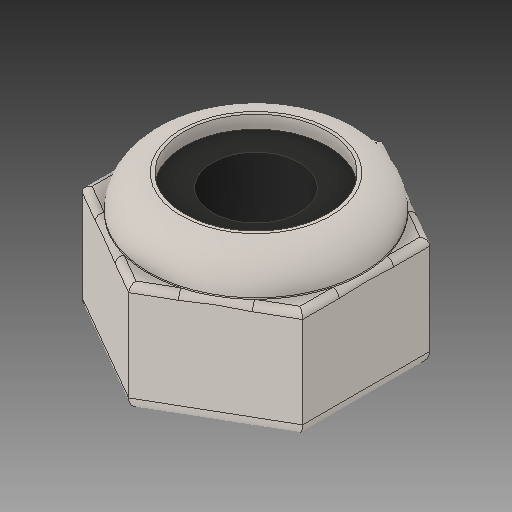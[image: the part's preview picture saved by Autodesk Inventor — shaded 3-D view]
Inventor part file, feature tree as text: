
AUTODESK INVENTOR PART (.ipt)
format: ipt  version: 2017 (Build 210142000, 142)  size: 227,328 bytes
history: native  units: in
note: dims shown in document units (in); Inventor stores cm internally (conversion verified against a paired STEP export)
features: fillet x1
ambient origin geometry x8: Origin, YZ Plane, XZ Plane, XY Plane, X Axis, Y Axis, Z Axis, Center Point
bodies: Solid1 (feature_tree)
feature tree (1):
  fillet  "Fillet6"  [1 undecoded]
note: 1 required parameter value undecoded (feature->parameter linkage not recoverable at this tier; creation-order binding heuristic only, values carry confidence <= 0.55)
